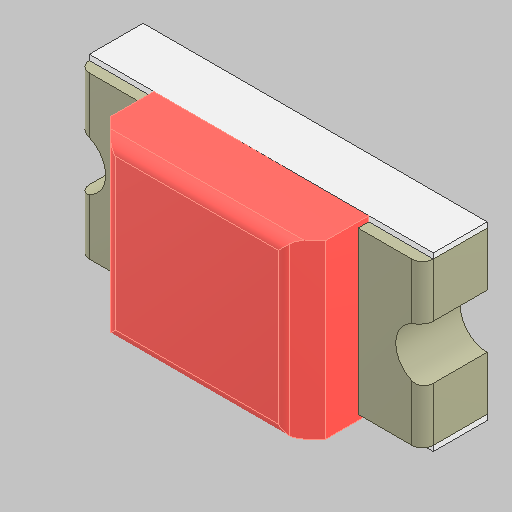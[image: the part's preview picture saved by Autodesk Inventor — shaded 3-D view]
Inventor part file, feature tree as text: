
AUTODESK INVENTOR PART (.ipt)
format: ipt  version: 2023.5 (Build 275446000, 446)  size: 160,256 bytes
history: native  units: in
note: dims shown in document units (in); Inventor stores cm internally (conversion verified against a paired STEP export)
features: fillet x2, other x2
ambient origin geometry x8: Origin, YZ Plane, XZ Plane, XY Plane, X Axis, Y Axis, Z Axis, Center Point
bodies: Solid1 (feature_tree), Solid2 (feature_tree), Solid3 (feature_tree), Solid4 (feature_tree)
feature tree (4):
  fillet  "Fillet001_(Solid)001:1"  [1 undecoded]
  fillet  "Fillet001_(Solid):1"  [1 undecoded]
  other  "Lens:1"
  other  "Base:1"
note: 2 required parameter values undecoded (feature->parameter linkage not recoverable at this tier; creation-order binding heuristic only, values carry confidence <= 0.55)
